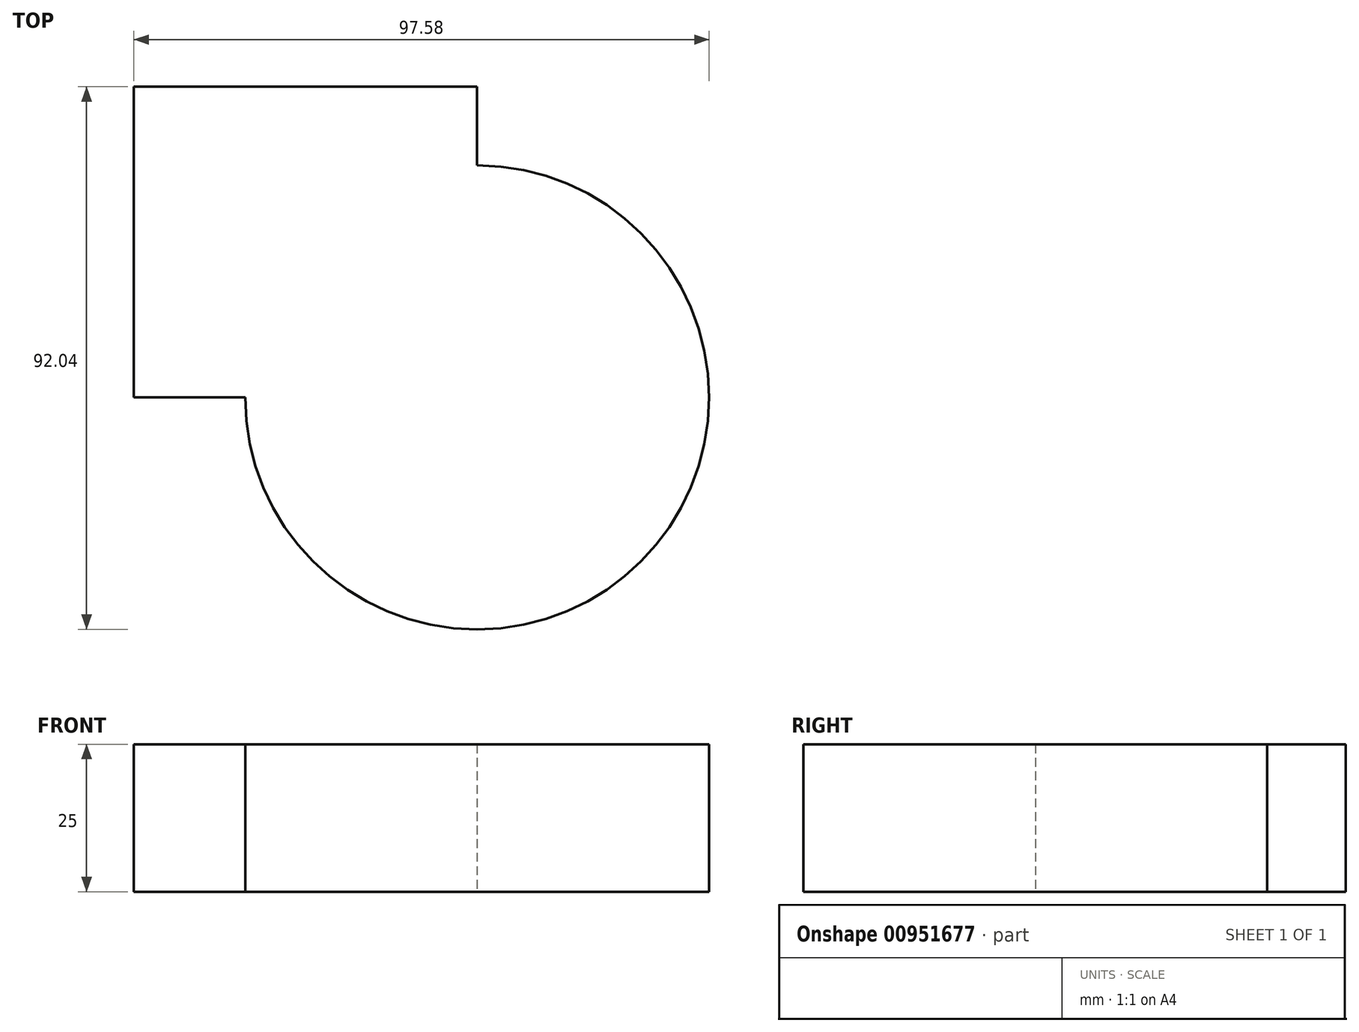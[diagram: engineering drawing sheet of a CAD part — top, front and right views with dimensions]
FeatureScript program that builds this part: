
annotation { "Feature Type Name" : "Feature", "Feature Type Description" : "" }
export const myFeature = defineFeature(function(context is Context, id is Id, definition is map)
    precondition{}
    {
        {
            var Q0;
            Q0=qCreatedBy(makeId("Top.planeOp"),FACE);
            var sketch = newSketch(context, id + "F0", { "sketchPlane" : qUnion([Q0])});
            skCircle(sketch, "E0", {"center": v(0, 0) * mm, "radius": 39.35 * mm});
            skLineSegment(sketch, "E1.bottom", {"start": v(0, 0) * mm, "end": v(-58.23, 0) * mm});
            skLineSegment(sketch, "E1.top", {"start": v(0, 52.69) * mm, "end": v(-58.23, 52.69) * mm});
            skLineSegment(sketch, "E1.left", {"start": v(0, 0) * mm, "end": v(0, 52.69) * mm});
            skLineSegment(sketch, "E1.right", {"start": v(-58.23, 0) * mm, "end": v(-58.23, 52.69) * mm});
            skSolve(sketch);
        }
        {
            var Q0;
            {var subQ1=sQuery(id+"F0.wireOp",EDGE,"E1.top");Q0=makeQuery(id+"F0.imprint","IMPRINT",FACE,{"disambiguationData":[TD([[makeQuery(id+"F0.imprint","IMPRINT",EDGE,{"derivedFrom":subQ1}),1.0]])]});}
            extrude(context, id + "F1", {"entities" : qUnion([Q0]), "depth" : 25 * mm, "offsetDistance" : 25 * mm});
        }
        {
            var Q0;
            {var subQ0=sQuery(id+"F0.wireOp",EDGE,"E1.bottom");var subQ1=sQuery(id+"F0.wireOp",EDGE,"E0");var subQ2=makeQuery(id+"F0.imprint","INTERSECT",VERTEX,{"derivedFrom":[subQ1,subQ0]});Q0=makeQuery(id+"F0.imprint","IMPRINT",FACE,{"disambiguationData":[TD([[makeQuery(id+"F0.imprint","IMPRINT",EDGE,{"disambiguationData":[TD([[subQ2,1.0]])],"derivedFrom":subQ1}),1.0]])]});}
            var Q1;
            {var subQ0=sQuery(id+"F0.wireOp",EDGE,"E1.bottom");var subQ1=sQuery(id+"F0.wireOp",EDGE,"E0");var subQ2=makeQuery(id+"F0.imprint","INTERSECT",VERTEX,{"derivedFrom":[subQ1,subQ0]});Q1=makeQuery(id+"F0.imprint","IMPRINT",FACE,{"disambiguationData":[TD([[makeQuery(id+"F0.imprint","IMPRINT",EDGE,{"disambiguationData":[TD([[subQ2,-1.0]])],"derivedFrom":subQ1}),1.0]])]});}
            extrude(context, id + "F2", {"entities" : qUnion([Q0, Q1]), "operationType" : NewBodyOperationType.ADD, "depth" : 25 * mm, "offsetDistance" : 25 * mm});
        }
    });
